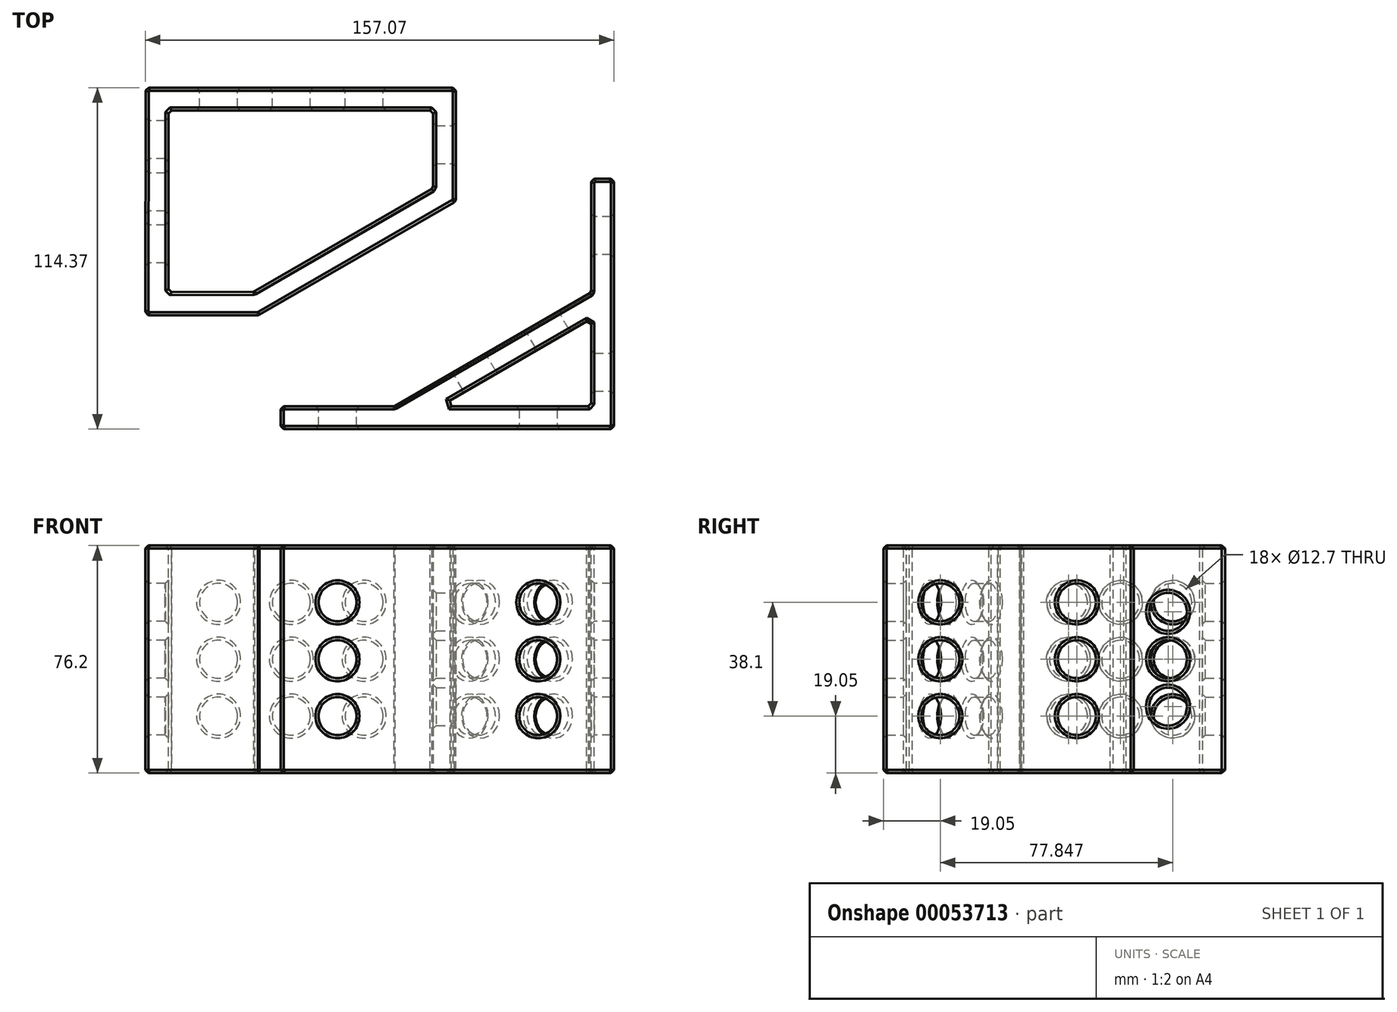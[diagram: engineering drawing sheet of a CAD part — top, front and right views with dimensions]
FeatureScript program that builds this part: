
annotation { "Feature Type Name" : "Feature", "Feature Type Description" : "" }
export const myFeature = defineFeature(function(context is Context, id is Id, definition is map)
    precondition{}
    {
        {
            var Q0;
            Q0=qCreatedBy(makeId("Top.planeOp"),FACE);
            var sketch = newSketch(context, id + "F0", { "sketchPlane" : qUnion([Q0])});
            skLineSegment(sketch, "E0", {"start": v(32.56, 38.1) * mm, "end": v(-33.43, 0) * mm});
            skLineSegment(sketch, "E1", {"start": v(-33.43, 0) * mm, "end": v(-71.53, 0) * mm});
            skLineSegment(sketch, "E2", {"start": v(-71.53, 0) * mm, "end": v(-71.53, -7.62) * mm});
            skLineSegment(sketch, "E3", {"start": v(-71.53, -7.62) * mm, "end": v(40.18, -7.62) * mm});
            skLineSegment(sketch, "E4", {"start": v(40.18, -7.62) * mm, "end": v(40.18, 76.2) * mm});
            skLineSegment(sketch, "E5", {"start": v(32.56, 38.1) * mm, "end": v(32.56, 76.2) * mm});
            skLineSegment(sketch, "E6", {"start": v(32.56, 76.2) * mm, "end": v(40.18, 76.2) * mm});
            skLineSegment(sketch, "E7", {"start": v(-3.8, 17.1) * mm, "end": v(0, 10.5) * mm, "construction": true});
            skLineSegment(sketch, "E8", {"start": v(-6.97, -7.62) * mm, "end": v(-6.97, 0) * mm, "construction": true});
            skLineSegment(sketch, "E9", {"start": v(40.18, 10.76) * mm, "end": v(32.56, 10.76) * mm, "construction": true});
            skLineSegment(sketch, "E10", {"start": v(32.56, 29.3) * mm, "end": v(-18.19, 0) * mm});
            skLineSegment(sketch, "E11", {"start": v(-18.19, 0) * mm, "end": v(32.56, 0) * mm});
            skLineSegment(sketch, "E12", {"start": v(32.56, 0) * mm, "end": v(32.56, 29.3) * mm});
            skSolve(sketch);
        }
        {
            var Q0;
            Q0=qCreatedBy(makeId("Top.planeOp"),FACE);
            var sketch = newSketch(context, id + "F1", { "sketchPlane" : qUnion([Q0])});
            skLineSegment(sketch, "E13", {"start": v(-12.8, 68.65) * mm, "end": v(-78.8, 30.55) * mm});
            skLineSegment(sketch, "E14", {"start": v(-78.8, 30.55) * mm, "end": v(-116.9, 30.55) * mm});
            skLineSegment(sketch, "E15", {"start": v(-12.8, 68.65) * mm, "end": v(-12.8, 106.75) * mm});
            skLineSegment(sketch, "E16", {"start": v(-12.8, 106.75) * mm, "end": v(-116.7, 106.75) * mm});
            skLineSegment(sketch, "E17", {"start": v(-116.7, 106.75) * mm, "end": v(-116.9, 30.55) * mm});
            skSolve(sketch);
        }
        {
            var Q0;
            Q0 = qSketchRegion(id + "F0", true);
            extrude(context, id + "F2", {"entities" : qUnion([Q0]), "depth" : 76.2 * mm});
        }
        {
            var Q0;
            Q0 = qSketchRegion(id + "F1", true);
            extrude(context, id + "F3", {"entities" : qUnion([Q0]), "depth" : 76.2 * mm});
        }
        {
            var Q0;
            Q0=makeQuery(id+"F3.opExtrude","CAP_FACE",FACE,{"disambiguationData":[OSD([sQuery(id+"F1.wireOp",EDGE,"E13"),sQuery(id+"F1.wireOp",EDGE,"E14"),sQuery(id+"F1.wireOp",EDGE,"E15"),sQuery(id+"F1.wireOp",EDGE,"E16"),sQuery(id+"F1.wireOp",EDGE,"E17")])],"isStart":false});
            var sketch = newSketch(context, id + "F4", { "sketchPlane" : qUnion([Q0])});
            skLineSegment(sketch, "E18", {"start": v(-64.75, 106.75) * mm, "end": v(-64.75, 99.13) * mm, "construction": true});
            skLineSegment(sketch, "E19", {"start": v(-116.78, 73.4) * mm, "end": v(-109.16, 73.37) * mm, "construction": true});
            skLineSegment(sketch, "E20", {"start": v(-97.84, 30.55) * mm, "end": v(-97.84, 38.17) * mm, "construction": true});
            skLineSegment(sketch, "E21", {"start": v(-12.8, 87.7) * mm, "end": v(-20.42, 87.7) * mm, "construction": true});
            skLineSegment(sketch, "E22", {"start": v(-45.8, 49.6) * mm, "end": v(-49.6, 56.2) * mm, "construction": true});
            skLineSegment(sketch, "E23", {"start": v(-64.75, 99.13) * mm, "end": v(-109.16, 99.13) * mm});
            skLineSegment(sketch, "E24", {"start": v(-109.16, 99.13) * mm, "end": v(-109.16, 38.17) * mm});
            skLineSegment(sketch, "E25", {"start": v(-64.75, 99.13) * mm, "end": v(-20.42, 99.13) * mm});
            skLineSegment(sketch, "E26", {"start": v(-20.42, 99.13) * mm, "end": v(-20.42, 73.05) * mm});
            skLineSegment(sketch, "E27", {"start": v(-20.42, 73.05) * mm, "end": v(-80.4, 38.42) * mm});
            skLineSegment(sketch, "E28", {"start": v(-109.16, 38.17) * mm, "end": v(-80.4, 38.42) * mm});
            skSolve(sketch);
        }
        {
            var Q0;
            Q0 = qSketchRegion(id + "F4", true);
            var Q1;
            Q1=makeQuery(id+"F3.opExtrude","CAP_FACE",FACE,{"disambiguationData":[OSD([sQuery(id+"F1.wireOp",EDGE,"E13"),sQuery(id+"F1.wireOp",EDGE,"E14"),sQuery(id+"F1.wireOp",EDGE,"E15"),sQuery(id+"F1.wireOp",EDGE,"E16"),sQuery(id+"F1.wireOp",EDGE,"E17")])],"isStart":true});
            extrude(context, id + "F5", {"entities" : qUnion([Q0]), "operationType" : NewBodyOperationType.REMOVE, "endBound" : BoundingType.UP_TO_SURFACE, "oppositeDirection" : true, "endBoundEntityFace" : qUnion([Q1]), "depth" : 25.4 * mm});
        }
        {
            var Q0;
            Q0=makeQuery(id+"F2.opExtrude","SWEPT_FACE",FACE,{"disambiguationData":[OSD([sQuery(id+"F0.wireOp",EDGE,"E0")])]});
            var sketch = newSketch(context, id + "F6", { "sketchPlane" : qUnion([Q0])});
            skLineSegment(sketch, "E29.bottom", {"start": v(28.95, 0) * mm, "end": v(-47.25, 0) * mm, "construction": true});
            skLineSegment(sketch, "E29.top", {"start": v(28.95, 76.2) * mm, "end": v(-47.25, 76.2) * mm, "construction": true});
            skLineSegment(sketch, "E29.left", {"start": v(28.95, 0) * mm, "end": v(28.95, 76.2) * mm, "construction": true});
            skLineSegment(sketch, "E29.right", {"start": v(-47.25, 0) * mm, "end": v(-47.25, 76.2) * mm, "construction": true});
            skLineSegment(sketch, "E30", {"start": v(-9.15, 0) * mm, "end": v(-9.15, 76.2) * mm, "construction": true});
            skLineSegment(sketch, "E31", {"start": v(28.95, 38.1) * mm, "end": v(-47.25, 38.1) * mm, "construction": true});
            skLineSegment(sketch, "E32", {"start": v(28.95, 38.1) * mm, "end": v(28.95, 0) * mm, "construction": true});
            skLineSegment(sketch, "E33", {"start": v(28.95, 19.05) * mm, "end": v(-47.25, 19.05) * mm, "construction": true});
            skLineSegment(sketch, "E34", {"start": v(28.95, 0) * mm, "end": v(-9.15, 0) * mm, "construction": true});
            skLineSegment(sketch, "E35", {"start": v(9.9, 0) * mm, "end": v(9.9, 76.2) * mm, "construction": true});
            skLineSegment(sketch, "E36", {"start": v(-9.15, 0) * mm, "end": v(-47.25, 0) * mm, "construction": true});
            skLineSegment(sketch, "E37", {"start": v(-28.2, 0) * mm, "end": v(-28.2, 76.2) * mm, "construction": true});
            skLineSegment(sketch, "E38", {"start": v(28.95, 38.1) * mm, "end": v(28.95, 76.2) * mm, "construction": true});
            skLineSegment(sketch, "E39", {"start": v(28.95, 57.15) * mm, "end": v(-47.25, 57.15) * mm, "construction": true});
            skCircle(sketch, "E40", {"center": v(-28.2, 57.15) * mm, "radius": 6.35 * mm});
            skCircle(sketch, "E41", {"center": v(-28.2, 38.1) * mm, "radius": 6.35 * mm});
            skCircle(sketch, "E42", {"center": v(-28.2, 19.05) * mm, "radius": 6.35 * mm});
            skLineSegment(sketch, "E43", {"start": v(0, 0) * mm, "end": v(0, 76.2) * mm, "construction": true});
            skCircle(sketch, "E44", {"center": v(0, 19.05) * mm, "radius": 6.35 * mm});
            skCircle(sketch, "E45", {"center": v(0, 38.1) * mm, "radius": 6.35 * mm});
            skCircle(sketch, "E46", {"center": v(0, 57.15) * mm, "radius": 6.35 * mm});
            skSolve(sketch);
        }
        {
            var Q0;
            Q0 = qSketchRegion(id + "F6", true);
            var Q1;
            Q1=makeQuery(id+"F2.opExtrude","SWEPT_FACE",FACE,{"disambiguationData":[OSD([sQuery(id+"F0.wireOp",EDGE,"E10")])]});
            extrude(context, id + "F7", {"entities" : qUnion([Q0]), "operationType" : NewBodyOperationType.REMOVE, "endBound" : BoundingType.UP_TO_SURFACE, "oppositeDirection" : true, "endBoundEntityFace" : qUnion([Q1]), "depth" : 25.4 * mm});
        }
        {
            var Q0;
            Q0=makeQuery(id+"F2.opExtrude","SWEPT_FACE",FACE,{"disambiguationData":[OSD([sQuery(id+"F0.wireOp",EDGE,"E1")])]});
            var sketch = newSketch(context, id + "F8", { "sketchPlane" : qUnion([Q0])});
            skLineSegment(sketch, "E47", {"start": v(71.53, 0) * mm, "end": v(52.48, 0) * mm, "construction": true});
            skLineSegment(sketch, "E48", {"start": v(52.48, 0) * mm, "end": v(33.43, 0) * mm, "construction": true});
            skLineSegment(sketch, "E49", {"start": v(33.43, 38.1) * mm, "end": v(33.43, 76.2) * mm, "construction": true});
            skLineSegment(sketch, "E50", {"start": v(33.43, 76.2) * mm, "end": v(52.48, 76.2) * mm, "construction": true});
            skLineSegment(sketch, "E51", {"start": v(52.48, 76.2) * mm, "end": v(71.53, 76.2) * mm, "construction": true});
            skLineSegment(sketch, "E52", {"start": v(71.53, 76.2) * mm, "end": v(71.53, 38.1) * mm, "construction": true});
            skLineSegment(sketch, "E53", {"start": v(71.53, 38.1) * mm, "end": v(71.53, 0) * mm, "construction": true});
            skLineSegment(sketch, "E54", {"start": v(52.48, 0) * mm, "end": v(52.48, 76.2) * mm, "construction": true});
            skLineSegment(sketch, "E55", {"start": v(71.53, 38.1) * mm, "end": v(33.43, 38.1) * mm, "construction": true});
            skLineSegment(sketch, "E56", {"start": v(33.43, 0) * mm, "end": v(33.43, 38.1) * mm, "construction": true});
            skLineSegment(sketch, "E57", {"start": v(33.43, 19.05) * mm, "end": v(71.53, 19.05) * mm, "construction": true});
            skLineSegment(sketch, "E58", {"start": v(71.53, 57.15) * mm, "end": v(33.43, 57.15) * mm, "construction": true});
            skCircle(sketch, "E59", {"center": v(52.48, 19.05) * mm, "radius": 6.35 * mm});
            skCircle(sketch, "E60", {"center": v(52.48, 38.1) * mm, "radius": 6.35 * mm});
            skCircle(sketch, "E61", {"center": v(52.48, 57.15) * mm, "radius": 6.35 * mm});
            skSolve(sketch);
        }
        {
            var Q0;
            Q0 = qSketchRegion(id + "F8", true);
            extrude(context, id + "F9", {"entities" : qUnion([Q0]), "operationType" : NewBodyOperationType.REMOVE, "oppositeDirection" : true, "depth" : 25.4 * mm});
        }
        {
            var Q0;
            Q0=makeQuery(id+"F2.opExtrude","SWEPT_FACE",FACE,{"disambiguationData":[OSD([sQuery(id+"F0.wireOp",EDGE,"E5")])]});
            var sketch = newSketch(context, id + "F10", { "sketchPlane" : qUnion([Q0])});
            skLineSegment(sketch, "E62", {"start": v(-38.1, 0) * mm, "end": v(-57.15, 0) * mm, "construction": true});
            skLineSegment(sketch, "E63", {"start": v(-57.15, 0) * mm, "end": v(-76.2, 0) * mm, "construction": true});
            skLineSegment(sketch, "E64", {"start": v(-76.2, 0) * mm, "end": v(-76.2, 38.1) * mm, "construction": true});
            skLineSegment(sketch, "E65", {"start": v(-76.2, 38.1) * mm, "end": v(-76.2, 76.2) * mm, "construction": true});
            skLineSegment(sketch, "E66", {"start": v(-76.2, 76.2) * mm, "end": v(-57.15, 76.2) * mm, "construction": true});
            skLineSegment(sketch, "E67", {"start": v(-57.15, 76.2) * mm, "end": v(-38.1, 76.2) * mm, "construction": true});
            skLineSegment(sketch, "E68", {"start": v(-38.1, 76.2) * mm, "end": v(-38.1, 38.1) * mm, "construction": true});
            skLineSegment(sketch, "E69", {"start": v(-38.1, 38.1) * mm, "end": v(-38.1, 0) * mm, "construction": true});
            skLineSegment(sketch, "E70", {"start": v(-57.15, 0) * mm, "end": v(-57.15, 76.2) * mm, "construction": true});
            skLineSegment(sketch, "E71", {"start": v(-38.1, 38.1) * mm, "end": v(-76.2, 38.1) * mm, "construction": true});
            skLineSegment(sketch, "E72", {"start": v(-76.2, 38.1) * mm, "end": v(-76.2, 0) * mm, "construction": true});
            skLineSegment(sketch, "E73", {"start": v(-76.2, 19.05) * mm, "end": v(-38.1, 19.05) * mm, "construction": true});
            skLineSegment(sketch, "E74", {"start": v(-38.1, 57.15) * mm, "end": v(-76.2, 57.15) * mm, "construction": true});
            skCircle(sketch, "E75", {"center": v(-57.15, 19.05) * mm, "radius": 6.35 * mm});
            skCircle(sketch, "E76", {"center": v(-57.15, 38.1) * mm, "radius": 6.35 * mm});
            skCircle(sketch, "E77", {"center": v(-57.15, 57.15) * mm, "radius": 6.35 * mm});
            skSolve(sketch);
        }
        {
            var Q0;
            Q0 = qSketchRegion(id + "F10", true);
            extrude(context, id + "F11", {"entities" : qUnion([Q0]), "operationType" : NewBodyOperationType.REMOVE, "oppositeDirection" : true, "depth" : 25.4 * mm});
        }
        {
            var Q0;
            Q0=makeQuery(id+"F2.opExtrude","SWEPT_FACE",FACE,{"disambiguationData":[OSD([sQuery(id+"F0.wireOp",EDGE,"E3")])]});
            var sketch = newSketch(context, id + "F12", { "sketchPlane" : qUnion([Q0])});
            skLineSegment(sketch, "E78", {"start": v(40.18, 76.2) * mm, "end": v(40.18, 38.1) * mm, "construction": true});
            skLineSegment(sketch, "E79", {"start": v(40.18, 38.1) * mm, "end": v(14.78, 38.1) * mm, "construction": true});
            skLineSegment(sketch, "E80", {"start": v(40.18, 0) * mm, "end": v(40.18, 38.1) * mm, "construction": true});
            skLineSegment(sketch, "E81", {"start": v(40.18, 19.05) * mm, "end": v(14.78, 19.05) * mm, "construction": true});
            skLineSegment(sketch, "E82", {"start": v(40.18, 38.1) * mm, "end": v(40.18, 57.15) * mm, "construction": true});
            skLineSegment(sketch, "E83", {"start": v(40.18, 57.15) * mm, "end": v(14.78, 57.15) * mm, "construction": true});
            skCircle(sketch, "E84", {"center": v(14.78, 19.05) * mm, "radius": 6.35 * mm});
            skCircle(sketch, "E85", {"center": v(14.78, 38.1) * mm, "radius": 6.35 * mm});
            skCircle(sketch, "E86", {"center": v(14.78, 57.15) * mm, "radius": 6.35 * mm});
            skSolve(sketch);
        }
        {
            var Q0;
            Q0 = qSketchRegion(id + "F12", true);
            var Q1;
            Q1=makeQuery(id+"F2.opExtrude","SWEPT_FACE",FACE,{"disambiguationData":[OSD([sQuery(id+"F0.wireOp",EDGE,"E11")])]});
            extrude(context, id + "F13", {"entities" : qUnion([Q0]), "operationType" : NewBodyOperationType.REMOVE, "endBound" : BoundingType.UP_TO_SURFACE, "oppositeDirection" : true, "endBoundEntityFace" : qUnion([Q1]), "depth" : 25.4 * mm});
        }
        {
            var Q0;
            Q0=makeQuery(id+"F2.opExtrude","SWEPT_FACE",FACE,{"disambiguationData":[OSD([sQuery(id+"F0.wireOp",EDGE,"E4")])]});
            var sketch = newSketch(context, id + "F14", { "sketchPlane" : qUnion([Q0])});
            skLineSegment(sketch, "E87", {"start": v(57.15, 57.15) * mm, "end": v(-7.62, 57.15) * mm, "construction": true});
            skLineSegment(sketch, "E88", {"start": v(57.15, 38.1) * mm, "end": v(-7.62, 38.1) * mm, "construction": true});
            skLineSegment(sketch, "E89", {"start": v(57.15, 19.05) * mm, "end": v(-7.62, 19.05) * mm, "construction": true});
            skLineSegment(sketch, "E90", {"start": v(-7.62, 76.2) * mm, "end": v(11.43, 76.2) * mm, "construction": true});
            skCircle(sketch, "E91", {"center": v(11.43, 57.15) * mm, "radius": 6.35 * mm});
            skPoint(sketch, "E91.centerSnap0", {"position": v(24.77, 57.15) * mm});
            skCircle(sketch, "E92", {"center": v(11.43, 38.1) * mm, "radius": 6.35 * mm});
            skCircle(sketch, "E93", {"center": v(11.43, 19.05) * mm, "radius": 6.35 * mm});
            skSolve(sketch);
        }
        {
            var Q0;
            Q0 = qSketchRegion(id + "F14", true);
            var Q1;
            Q1=makeQuery(id+"F2.opExtrude","SWEPT_FACE",FACE,{"disambiguationData":[OSD([sQuery(id+"F0.wireOp",EDGE,"E12")])]});
            extrude(context, id + "F15", {"entities" : qUnion([Q0]), "operationType" : NewBodyOperationType.REMOVE, "endBound" : BoundingType.UP_TO_SURFACE, "oppositeDirection" : true, "endBoundEntityFace" : qUnion([Q1]), "depth" : 25.4 * mm});
        }
        {
            var Q0;
            Q0=makeQuery(id+"F3.opExtrude","SWEPT_FACE",FACE,{"disambiguationData":[OSD([sQuery(id+"F1.wireOp",EDGE,"E15")])]});
            var sketch = newSketch(context, id + "F16", { "sketchPlane" : qUnion([Q0])});
            skLineSegment(sketch, "E94", {"start": v(106.75, 38.1) * mm, "end": v(68.65, 38.1) * mm, "construction": true});
            skLineSegment(sketch, "E95", {"start": v(106.75, 53.98) * mm, "end": v(68.65, 53.98) * mm, "construction": true});
            skLineSegment(sketch, "E96", {"start": v(68.65, 22.23) * mm, "end": v(106.75, 22.23) * mm, "construction": true});
            skCircle(sketch, "E97", {"center": v(87.7, 53.98) * mm, "radius": 6.35 * mm});
            skCircle(sketch, "E98", {"center": v(87.7, 38.1) * mm, "radius": 6.35 * mm});
            skCircle(sketch, "E99", {"center": v(87.7, 22.23) * mm, "radius": 6.35 * mm});
            skSolve(sketch);
        }
        {
            var Q0;
            Q0 = qSketchRegion(id + "F16", true);
            var Q1;
            Q1=makeQuery(id+"F5.boolean.opBoolean","COPY",FACE,{"derivedFrom":makeQuery(id+"F5.opExtrude","SWEPT_FACE",FACE,{"disambiguationData":[OSD([sQuery(id+"F4.wireOp",EDGE,"E26")])]})});
            extrude(context, id + "F17", {"entities" : qUnion([Q0]), "operationType" : NewBodyOperationType.REMOVE, "endBound" : BoundingType.UP_TO_SURFACE, "oppositeDirection" : true, "endBoundEntityFace" : qUnion([Q1]), "depth" : 25.4 * mm});
        }
        {
            var Q0;
            Q0=makeQuery(id+"F3.opExtrude","SWEPT_FACE",FACE,{"disambiguationData":[OSD([sQuery(id+"F1.wireOp",EDGE,"E16")])]});
            var sketch = newSketch(context, id + "F18", { "sketchPlane" : qUnion([Q0])});
            skLineSegment(sketch, "E100", {"start": v(116.7, 38.1) * mm, "end": v(116.7, 0) * mm, "construction": true});
            skLineSegment(sketch, "E101", {"start": v(92.3, 0) * mm, "end": v(92.3, 76.2) * mm, "construction": true});
            skLineSegment(sketch, "E102", {"start": v(43.54, 76.2) * mm, "end": v(43.54, 0) * mm, "construction": true});
            skLineSegment(sketch, "E103", {"start": v(64.75, 0) * mm, "end": v(64.75, 76.2) * mm, "construction": true});
            skLineSegment(sketch, "E104", {"start": v(116.7, 19.05) * mm, "end": v(19.15, 19.05) * mm, "construction": true});
            skLineSegment(sketch, "E105", {"start": v(116.7, 57.15) * mm, "end": v(19.15, 57.15) * mm, "construction": true});
            skLineSegment(sketch, "E106", {"start": v(116.7, 38.1) * mm, "end": v(19.15, 38.1) * mm, "construction": true});
            skCircle(sketch, "E107", {"center": v(92.3, 19.05) * mm, "radius": 6.35 * mm});
            skCircle(sketch, "E108", {"center": v(67.92, 19.05) * mm, "radius": 6.35 * mm});
            skCircle(sketch, "E109", {"center": v(43.54, 19.05) * mm, "radius": 6.35 * mm});
            skCircle(sketch, "E110", {"center": v(92.3, 38.1) * mm, "radius": 6.35 * mm});
            skCircle(sketch, "E111", {"center": v(67.92, 38.1) * mm, "radius": 6.35 * mm});
            skCircle(sketch, "E112", {"center": v(43.54, 38.1) * mm, "radius": 6.35 * mm});
            skCircle(sketch, "E113", {"center": v(92.3, 57.15) * mm, "radius": 6.35 * mm});
            skCircle(sketch, "E114", {"center": v(67.92, 57.15) * mm, "radius": 6.35 * mm});
            skCircle(sketch, "E115", {"center": v(43.54, 57.15) * mm, "radius": 6.35 * mm});
            skSolve(sketch);
        }
        {
            var Q0;
            Q0 = qSketchRegion(id + "F18", true);
            var Q1;
            Q1=makeQuery(id+"F5.boolean.opBoolean","COPY",FACE,{"derivedFrom":makeQuery(id+"F5.opExtrude","SWEPT_FACE",FACE,{"disambiguationData":[OSD([sQuery(id+"F4.wireOp",EDGE,"E23"),sQuery(id+"F4.wireOp",EDGE,"E25")])]})});
            extrude(context, id + "F19", {"entities" : qUnion([Q0]), "operationType" : NewBodyOperationType.REMOVE, "endBound" : BoundingType.UP_TO_SURFACE, "oppositeDirection" : true, "endBoundEntityFace" : qUnion([Q1]), "depth" : 25.4 * mm});
        }
        {
            var Q0;
            Q0=makeQuery(id+"F3.opExtrude","SWEPT_FACE",FACE,{"disambiguationData":[OSD([sQuery(id+"F1.wireOp",EDGE,"E17")])]});
            var sketch = newSketch(context, id + "F20", { "sketchPlane" : qUnion([Q0])});
            skCircle(sketch, "E116", {"center": v(-88.98, 19.05) * mm, "radius": 6.35 * mm});
            skCircle(sketch, "E117", {"center": v(-88.98, 38.1) * mm, "radius": 6.35 * mm});
            skCircle(sketch, "E118", {"center": v(-88.98, 57.15) * mm, "radius": 6.35 * mm});
            skCircle(sketch, "E119", {"center": v(-71.51, 19.05) * mm, "radius": 6.35 * mm});
            skCircle(sketch, "E120", {"center": v(-71.51, 38.1) * mm, "radius": 6.35 * mm});
            skCircle(sketch, "E121", {"center": v(-71.51, 57.15) * mm, "radius": 6.35 * mm});
            skCircle(sketch, "E122", {"center": v(-54.05, 19.05) * mm, "radius": 6.35 * mm});
            skCircle(sketch, "E123", {"center": v(-54.05, 38.1) * mm, "radius": 6.35 * mm});
            skCircle(sketch, "E124", {"center": v(-54.05, 57.15) * mm, "radius": 6.35 * mm});
            skSolve(sketch);
        }
        {
            var Q0;
            Q0 = qSketchRegion(id + "F20", true);
            var Q1;
            Q1=makeQuery(id+"F5.boolean.opBoolean","COPY",FACE,{"derivedFrom":makeQuery(id+"F5.opExtrude","SWEPT_FACE",FACE,{"disambiguationData":[OSD([sQuery(id+"F4.wireOp",EDGE,"E24")])]})});
            extrude(context, id + "F21", {"entities" : qUnion([Q0]), "operationType" : NewBodyOperationType.REMOVE, "endBound" : BoundingType.UP_TO_SURFACE, "oppositeDirection" : true, "endBoundEntityFace" : qUnion([Q1]), "depth" : 25.4 * mm});
        }
        {
            var Q0;
            Q0=makeQuery(id+"F17.boolean.opBoolean","COPY",FACE,{"derivedFrom":makeQuery(id+"F17.opExtrude","SWEPT_FACE",FACE,{"disambiguationData":[OSD([sQuery(id+"F16.wireOp",EDGE,"E99")])]})});
            var Q1;
            Q1=makeQuery(id+"F17.boolean.opBoolean","COPY",FACE,{"derivedFrom":makeQuery(id+"F17.opExtrude","SWEPT_FACE",FACE,{"disambiguationData":[OSD([sQuery(id+"F16.wireOp",EDGE,"E98")])]})});
            var Q2;
            Q2=makeQuery(id+"F17.boolean.opBoolean","COPY",FACE,{"derivedFrom":makeQuery(id+"F17.opExtrude","SWEPT_FACE",FACE,{"disambiguationData":[OSD([sQuery(id+"F16.wireOp",EDGE,"E97")])]})});
            chamfer(context, id + "F22", {"entities" : qUnion([Q0, Q1, Q2]), "width" : 1.02 * mm, "tangentPropagation" : true});
        }
        {
            var Q0;
            Q0=makeQuery(id+"F19.boolean.opBoolean","COPY",EDGE,{"derivedFrom":makeQuery(id+"F19.opExtrude","CAP_EDGE",EDGE,{"disambiguationData":[OSD([sQuery(id+"F18.wireOp",EDGE,"E115")])],"isStart":true})});
            var Q1;
            Q1=makeQuery(id+"F19.boolean.opBoolean","COPY",FACE,{"derivedFrom":makeQuery(id+"F19.opExtrude","SWEPT_FACE",FACE,{"disambiguationData":[OSD([sQuery(id+"F18.wireOp",EDGE,"E115")])]})});
            var Q2;
            Q2=makeQuery(id+"F19.boolean.opBoolean","COPY",FACE,{"derivedFrom":makeQuery(id+"F19.opExtrude","SWEPT_FACE",FACE,{"disambiguationData":[OSD([sQuery(id+"F18.wireOp",EDGE,"E114")])]})});
            var Q3;
            Q3=makeQuery(id+"F19.boolean.opBoolean","COPY",FACE,{"derivedFrom":makeQuery(id+"F19.opExtrude","SWEPT_FACE",FACE,{"disambiguationData":[OSD([sQuery(id+"F18.wireOp",EDGE,"E113")])]})});
            var Q4;
            Q4=makeQuery(id+"F19.boolean.opBoolean","COPY",FACE,{"derivedFrom":makeQuery(id+"F19.opExtrude","SWEPT_FACE",FACE,{"disambiguationData":[OSD([sQuery(id+"F18.wireOp",EDGE,"E110")])]})});
            var Q5;
            Q5=makeQuery(id+"F19.boolean.opBoolean","COPY",FACE,{"derivedFrom":makeQuery(id+"F19.opExtrude","SWEPT_FACE",FACE,{"disambiguationData":[OSD([sQuery(id+"F18.wireOp",EDGE,"E107")])]})});
            var Q6;
            Q6=makeQuery(id+"F19.boolean.opBoolean","COPY",FACE,{"derivedFrom":makeQuery(id+"F19.opExtrude","SWEPT_FACE",FACE,{"disambiguationData":[OSD([sQuery(id+"F18.wireOp",EDGE,"E111")])]})});
            var Q7;
            Q7=makeQuery(id+"F19.boolean.opBoolean","COPY",FACE,{"derivedFrom":makeQuery(id+"F19.opExtrude","SWEPT_FACE",FACE,{"disambiguationData":[OSD([sQuery(id+"F18.wireOp",EDGE,"E112")])]})});
            var Q8;
            Q8=makeQuery(id+"F19.boolean.opBoolean","COPY",FACE,{"derivedFrom":makeQuery(id+"F19.opExtrude","SWEPT_FACE",FACE,{"disambiguationData":[OSD([sQuery(id+"F18.wireOp",EDGE,"E109")])]})});
            var Q9;
            Q9=makeQuery(id+"F19.boolean.opBoolean","COPY",FACE,{"derivedFrom":makeQuery(id+"F19.opExtrude","SWEPT_FACE",FACE,{"disambiguationData":[OSD([sQuery(id+"F18.wireOp",EDGE,"E108")])]})});
            chamfer(context, id + "F23", {"entities" : qUnion([Q0, Q1, Q2, Q3, Q4, Q5, Q6, Q7, Q8, Q9]), "width" : 1.02 * mm, "tangentPropagation" : true});
        }
        {
            var Q0;
            Q0=makeQuery(id+"F21.boolean.opBoolean","COPY",FACE,{"derivedFrom":makeQuery(id+"F21.opExtrude","SWEPT_FACE",FACE,{"disambiguationData":[OSD([sQuery(id+"F20.wireOp",EDGE,"E122")])]})});
            var Q1;
            Q1=makeQuery(id+"F21.boolean.opBoolean","COPY",FACE,{"derivedFrom":makeQuery(id+"F21.opExtrude","SWEPT_FACE",FACE,{"disambiguationData":[OSD([sQuery(id+"F20.wireOp",EDGE,"E119")])]})});
            var Q2;
            Q2=makeQuery(id+"F21.boolean.opBoolean","COPY",FACE,{"derivedFrom":makeQuery(id+"F21.opExtrude","SWEPT_FACE",FACE,{"disambiguationData":[OSD([sQuery(id+"F20.wireOp",EDGE,"E116")])]})});
            var Q3;
            Q3=makeQuery(id+"F21.boolean.opBoolean","COPY",FACE,{"derivedFrom":makeQuery(id+"F21.opExtrude","SWEPT_FACE",FACE,{"disambiguationData":[OSD([sQuery(id+"F20.wireOp",EDGE,"E117")])]})});
            var Q4;
            Q4=makeQuery(id+"F21.boolean.opBoolean","COPY",FACE,{"derivedFrom":makeQuery(id+"F21.opExtrude","SWEPT_FACE",FACE,{"disambiguationData":[OSD([sQuery(id+"F20.wireOp",EDGE,"E120")])]})});
            var Q5;
            Q5=makeQuery(id+"F21.boolean.opBoolean","COPY",FACE,{"derivedFrom":makeQuery(id+"F21.opExtrude","SWEPT_FACE",FACE,{"disambiguationData":[OSD([sQuery(id+"F20.wireOp",EDGE,"E123")])]})});
            var Q6;
            Q6=makeQuery(id+"F21.boolean.opBoolean","COPY",FACE,{"derivedFrom":makeQuery(id+"F21.opExtrude","SWEPT_FACE",FACE,{"disambiguationData":[OSD([sQuery(id+"F20.wireOp",EDGE,"E124")])]})});
            var Q7;
            Q7=makeQuery(id+"F21.boolean.opBoolean","COPY",FACE,{"derivedFrom":makeQuery(id+"F21.opExtrude","SWEPT_FACE",FACE,{"disambiguationData":[OSD([sQuery(id+"F20.wireOp",EDGE,"E121")])]})});
            var Q8;
            Q8=makeQuery(id+"F21.boolean.opBoolean","COPY",FACE,{"derivedFrom":makeQuery(id+"F21.opExtrude","SWEPT_FACE",FACE,{"disambiguationData":[OSD([sQuery(id+"F20.wireOp",EDGE,"E118")])]})});
            chamfer(context, id + "F24", {"entities" : qUnion([Q0, Q1, Q2, Q3, Q4, Q5, Q6, Q7, Q8]), "width" : 1.02 * mm, "tangentPropagation" : true});
        }
        {
            var Q0;
            Q0=makeQuery(id+"F5.boolean.opBoolean","COPY",EDGE,{"derivedFrom":makeQuery(id+"F5.opExtrude","SWEPT_EDGE",EDGE,{"disambiguationData":[OSD([sQuery(id+"F4.wireOp",EDGE,"E24"),sQuery(id+"F4.wireOp",EDGE,"E28")])]})});
            var Q1;
            Q1=makeQuery(id+"F5.boolean.opBoolean","COPY",EDGE,{"derivedFrom":makeQuery(id+"F5.opExtrude","SWEPT_EDGE",EDGE,{"disambiguationData":[OSD([sQuery(id+"F4.wireOp",EDGE,"E27"),sQuery(id+"F4.wireOp",EDGE,"E28")])]})});
            var Q2;
            Q2=makeQuery(id+"F5.boolean.opBoolean","COPY",EDGE,{"derivedFrom":makeQuery(id+"F5.opExtrude","SWEPT_EDGE",EDGE,{"disambiguationData":[OSD([sQuery(id+"F4.wireOp",EDGE,"E26"),sQuery(id+"F4.wireOp",EDGE,"E27")])]})});
            var Q3;
            Q3=makeQuery(id+"F5.boolean.opBoolean","COPY",EDGE,{"derivedFrom":makeQuery(id+"F5.opExtrude","SWEPT_EDGE",EDGE,{"disambiguationData":[OSD([sQuery(id+"F4.wireOp",EDGE,"E25"),sQuery(id+"F4.wireOp",EDGE,"E26")])]})});
            var Q4;
            Q4=makeQuery(id+"F5.boolean.opBoolean","COPY",EDGE,{"derivedFrom":makeQuery(id+"F5.opExtrude","SWEPT_EDGE",EDGE,{"disambiguationData":[OSD([sQuery(id+"F4.wireOp",EDGE,"E23"),sQuery(id+"F4.wireOp",EDGE,"E24")])]})});
            chamfer(context, id + "F25", {"entities" : qUnion([Q0, Q1, Q2, Q3, Q4]), "width" : 1.02 * mm, "tangentPropagation" : true});
        }
        {
            var Q0;
            Q0=makeQuery(id+"F5.boolean.opBoolean","COPY",EDGE,{"derivedFrom":makeQuery(id+"F5.opExtrude","SWEPT_EDGE",EDGE,{"disambiguationData":[OSD([sQuery(id+"F4.wireOp",EDGE,"E25"),sQuery(id+"F4.wireOp",EDGE,"E26")])]})});
            var Q1;
            Q1=makeQuery(id+"F3.opExtrude","SWEPT_EDGE",EDGE,{"disambiguationData":[OSD([sQuery(id+"F1.wireOp",EDGE,"E14"),sQuery(id+"F1.wireOp",EDGE,"E17")])]});
            var Q2;
            Q2=makeQuery(id+"F3.opExtrude","SWEPT_EDGE",EDGE,{"disambiguationData":[OSD([sQuery(id+"F1.wireOp",EDGE,"E13"),sQuery(id+"F1.wireOp",EDGE,"E14")])]});
            var Q3;
            Q3=makeQuery(id+"F3.opExtrude","SWEPT_EDGE",EDGE,{"disambiguationData":[OSD([sQuery(id+"F1.wireOp",EDGE,"E13"),sQuery(id+"F1.wireOp",EDGE,"E15")])]});
            var Q4;
            Q4=makeQuery(id+"F5.boolean.opBoolean","COPY",EDGE,{"derivedFrom":makeQuery(id+"F5.opExtrude","SWEPT_EDGE",EDGE,{"disambiguationData":[OSD([sQuery(id+"F4.wireOp",EDGE,"E23"),sQuery(id+"F4.wireOp",EDGE,"E24")])]})});
            var Q5;
            Q5=makeQuery(id+"F3.opExtrude","SWEPT_EDGE",EDGE,{"disambiguationData":[OSD([sQuery(id+"F1.wireOp",EDGE,"E15"),sQuery(id+"F1.wireOp",EDGE,"E16")])]});
            var Q6;
            Q6=makeQuery(id+"F3.opExtrude","SWEPT_EDGE",EDGE,{"disambiguationData":[OSD([sQuery(id+"F1.wireOp",EDGE,"E16"),sQuery(id+"F1.wireOp",EDGE,"E17")])]});
            chamfer(context, id + "F26", {"entities" : qUnion([Q0, Q1, Q2, Q3, Q4, Q5, Q6]), "width" : 1.02 * mm, "tangentPropagation" : true});
        }
        {
            var Q0;
            Q0=makeQuery(id+"F3.opExtrude","CAP_FACE",FACE,{"disambiguationData":[OSD([sQuery(id+"F1.wireOp",EDGE,"E13"),sQuery(id+"F1.wireOp",EDGE,"E14"),sQuery(id+"F1.wireOp",EDGE,"E15"),sQuery(id+"F1.wireOp",EDGE,"E16"),sQuery(id+"F1.wireOp",EDGE,"E17")])],"isStart":false});
            var Q1;
            Q1=makeQuery(id+"F3.opExtrude","CAP_FACE",FACE,{"disambiguationData":[OSD([sQuery(id+"F1.wireOp",EDGE,"E13"),sQuery(id+"F1.wireOp",EDGE,"E14"),sQuery(id+"F1.wireOp",EDGE,"E15"),sQuery(id+"F1.wireOp",EDGE,"E16"),sQuery(id+"F1.wireOp",EDGE,"E17")])],"isStart":true});
            chamfer(context, id + "F27", {"entities" : qUnion([Q0, Q1]), "width" : 1.02 * mm, "tangentPropagation" : true});
        }
        {
            var Q0;
            Q0=makeQuery(id+"F9.boolean.opBoolean","COPY",FACE,{"derivedFrom":makeQuery(id+"F9.opExtrude","SWEPT_FACE",FACE,{"disambiguationData":[OSD([sQuery(id+"F8.wireOp",EDGE,"E59")])]})});
            var Q1;
            Q1=makeQuery(id+"F9.boolean.opBoolean","COPY",FACE,{"derivedFrom":makeQuery(id+"F9.opExtrude","SWEPT_FACE",FACE,{"disambiguationData":[OSD([sQuery(id+"F8.wireOp",EDGE,"E60")])]})});
            var Q2;
            Q2=makeQuery(id+"F9.boolean.opBoolean","COPY",FACE,{"derivedFrom":makeQuery(id+"F9.opExtrude","SWEPT_FACE",FACE,{"disambiguationData":[OSD([sQuery(id+"F8.wireOp",EDGE,"E61")])]})});
            chamfer(context, id + "F28", {"entities" : qUnion([Q0, Q1, Q2]), "width" : 1.02 * mm, "tangentPropagation" : true});
        }
        {
            var Q0;
            Q0=makeQuery(id+"F11.boolean.opBoolean","COPY",FACE,{"derivedFrom":makeQuery(id+"F11.opExtrude","SWEPT_FACE",FACE,{"disambiguationData":[OSD([sQuery(id+"F10.wireOp",EDGE,"E75")])]})});
            var Q1;
            Q1=makeQuery(id+"F11.boolean.opBoolean","COPY",FACE,{"derivedFrom":makeQuery(id+"F11.opExtrude","SWEPT_FACE",FACE,{"disambiguationData":[OSD([sQuery(id+"F10.wireOp",EDGE,"E76")])]})});
            var Q2;
            Q2=makeQuery(id+"F11.boolean.opBoolean","COPY",FACE,{"derivedFrom":makeQuery(id+"F11.opExtrude","SWEPT_FACE",FACE,{"disambiguationData":[OSD([sQuery(id+"F10.wireOp",EDGE,"E77")])]})});
            chamfer(context, id + "F29", {"entities" : qUnion([Q0, Q1, Q2]), "width" : 1.02 * mm, "tangentPropagation" : true});
        }
        {
            var Q0;
            Q0=makeQuery(id+"F15.boolean.opBoolean","COPY",FACE,{"derivedFrom":makeQuery(id+"F15.opExtrude","SWEPT_FACE",FACE,{"disambiguationData":[OSD([sQuery(id+"F14.wireOp",EDGE,"E91")])]})});
            var Q1;
            Q1=makeQuery(id+"F15.boolean.opBoolean","COPY",FACE,{"derivedFrom":makeQuery(id+"F15.opExtrude","SWEPT_FACE",FACE,{"disambiguationData":[OSD([sQuery(id+"F14.wireOp",EDGE,"E92")])]})});
            var Q2;
            Q2=makeQuery(id+"F15.boolean.opBoolean","COPY",FACE,{"derivedFrom":makeQuery(id+"F15.opExtrude","SWEPT_FACE",FACE,{"disambiguationData":[OSD([sQuery(id+"F14.wireOp",EDGE,"E93")])]})});
            chamfer(context, id + "F30", {"entities" : qUnion([Q0, Q1, Q2]), "width" : 1.02 * mm, "tangentPropagation" : true});
        }
        {
            var Q0;
            Q0=makeQuery(id+"F13.boolean.opBoolean","COPY",FACE,{"derivedFrom":makeQuery(id+"F13.opExtrude","SWEPT_FACE",FACE,{"disambiguationData":[OSD([sQuery(id+"F12.wireOp",EDGE,"E86")])]})});
            var Q1;
            Q1=makeQuery(id+"F13.boolean.opBoolean","COPY",FACE,{"derivedFrom":makeQuery(id+"F13.opExtrude","SWEPT_FACE",FACE,{"disambiguationData":[OSD([sQuery(id+"F12.wireOp",EDGE,"E85")])]})});
            var Q2;
            Q2=makeQuery(id+"F13.boolean.opBoolean","COPY",FACE,{"derivedFrom":makeQuery(id+"F13.opExtrude","SWEPT_FACE",FACE,{"disambiguationData":[OSD([sQuery(id+"F12.wireOp",EDGE,"E84")])]})});
            chamfer(context, id + "F31", {"entities" : qUnion([Q0, Q1, Q2]), "width" : 1.02 * mm, "tangentPropagation" : true});
        }
        {
            var Q0;
            Q0=makeQuery(id+"F7.boolean.opBoolean","COPY",FACE,{"derivedFrom":makeQuery(id+"F7.opExtrude","SWEPT_FACE",FACE,{"disambiguationData":[OSD([sQuery(id+"F6.wireOp",EDGE,"E42")])]})});
            var Q1;
            Q1=makeQuery(id+"F7.boolean.opBoolean","COPY",FACE,{"derivedFrom":makeQuery(id+"F7.opExtrude","SWEPT_FACE",FACE,{"disambiguationData":[OSD([sQuery(id+"F6.wireOp",EDGE,"E41")])]})});
            var Q2;
            Q2=makeQuery(id+"F7.boolean.opBoolean","COPY",FACE,{"derivedFrom":makeQuery(id+"F7.opExtrude","SWEPT_FACE",FACE,{"disambiguationData":[OSD([sQuery(id+"F6.wireOp",EDGE,"E40")])]})});
            var Q3;
            Q3=makeQuery(id+"F7.boolean.opBoolean","COPY",FACE,{"derivedFrom":makeQuery(id+"F7.opExtrude","SWEPT_FACE",FACE,{"disambiguationData":[OSD([sQuery(id+"F6.wireOp",EDGE,"E44")])]})});
            var Q4;
            Q4=makeQuery(id+"F7.boolean.opBoolean","COPY",FACE,{"derivedFrom":makeQuery(id+"F7.opExtrude","SWEPT_FACE",FACE,{"disambiguationData":[OSD([sQuery(id+"F6.wireOp",EDGE,"E45")])]})});
            var Q5;
            Q5=makeQuery(id+"F7.boolean.opBoolean","COPY",FACE,{"derivedFrom":makeQuery(id+"F7.opExtrude","SWEPT_FACE",FACE,{"disambiguationData":[OSD([sQuery(id+"F6.wireOp",EDGE,"E46")])]})});
            chamfer(context, id + "F32", {"entities" : qUnion([Q0, Q1, Q2, Q3, Q4, Q5]), "width" : 1.02 * mm, "tangentPropagation" : true});
        }
        {
            var Q0;
            Q0=makeQuery(id+"F2.opExtrude","SWEPT_EDGE",EDGE,{"disambiguationData":[OSD([sQuery(id+"F0.wireOp",EDGE,"E2"),sQuery(id+"F0.wireOp",EDGE,"E3")])]});
            var Q1;
            Q1=makeQuery(id+"F2.opExtrude","SWEPT_EDGE",EDGE,{"disambiguationData":[OSD([sQuery(id+"F0.wireOp",EDGE,"E1"),sQuery(id+"F0.wireOp",EDGE,"E2")])]});
            var Q2;
            Q2=makeQuery(id+"F2.opExtrude","SWEPT_EDGE",EDGE,{"disambiguationData":[OSD([sQuery(id+"F0.wireOp",EDGE,"E0"),sQuery(id+"F0.wireOp",EDGE,"E1")])]});
            var Q3;
            Q3=makeQuery(id+"F2.opExtrude","SWEPT_EDGE",EDGE,{"disambiguationData":[OSD([sQuery(id+"F0.wireOp",EDGE,"E0"),sQuery(id+"F0.wireOp",EDGE,"E5")])]});
            var Q4;
            Q4=makeQuery(id+"F2.opExtrude","SWEPT_EDGE",EDGE,{"disambiguationData":[OSD([sQuery(id+"F0.wireOp",EDGE,"E5"),sQuery(id+"F0.wireOp",EDGE,"E6")])]});
            var Q5;
            Q5=makeQuery(id+"F2.opExtrude","SWEPT_EDGE",EDGE,{"disambiguationData":[OSD([sQuery(id+"F0.wireOp",EDGE,"E4"),sQuery(id+"F0.wireOp",EDGE,"E6")])]});
            var Q6;
            Q6=makeQuery(id+"F2.opExtrude","SWEPT_EDGE",EDGE,{"disambiguationData":[OSD([sQuery(id+"F0.wireOp",EDGE,"E3"),sQuery(id+"F0.wireOp",EDGE,"E4")])]});
            chamfer(context, id + "F33", {"entities" : qUnion([Q0, Q1, Q2, Q3, Q4, Q5, Q6]), "width" : 1.02 * mm, "tangentPropagation" : true});
        }
        {
            var Q0;
            Q0=makeQuery(id+"F2.opExtrude","SWEPT_EDGE",EDGE,{"disambiguationData":[OSD([sQuery(id+"F0.wireOp",EDGE,"E11"),sQuery(id+"F0.wireOp",EDGE,"E12")])]});
            var Q1;
            Q1=makeQuery(id+"F2.opExtrude","SWEPT_EDGE",EDGE,{"disambiguationData":[OSD([sQuery(id+"F0.wireOp",EDGE,"E10"),sQuery(id+"F0.wireOp",EDGE,"E11")])]});
            chamfer(context, id + "F34", {"entities" : qUnion([Q0, Q1]), "width" : 1.02 * mm, "tangentPropagation" : true});
        }
        {
            var Q0;
            Q0=makeQuery(id+"F2.opExtrude","SWEPT_EDGE",EDGE,{"disambiguationData":[OSD([sQuery(id+"F0.wireOp",EDGE,"E10"),sQuery(id+"F0.wireOp",EDGE,"E12")])]});
            chamfer(context, id + "F35", {"entities" : qUnion([Q0]), "width" : 1.02 * mm, "tangentPropagation" : true});
        }
        {
            var Q0;
            Q0=makeQuery(id+"F2.opExtrude","CAP_FACE",FACE,{"disambiguationData":[OSD([sQuery(id+"F0.wireOp",EDGE,"E0"),sQuery(id+"F0.wireOp",EDGE,"E1"),sQuery(id+"F0.wireOp",EDGE,"E2"),sQuery(id+"F0.wireOp",EDGE,"E3"),sQuery(id+"F0.wireOp",EDGE,"E4"),sQuery(id+"F0.wireOp",EDGE,"E5"),sQuery(id+"F0.wireOp",EDGE,"E6"),sQuery(id+"F0.wireOp",EDGE,"E10"),sQuery(id+"F0.wireOp",EDGE,"E11"),sQuery(id+"F0.wireOp",EDGE,"E12")])],"isStart":true});
            var Q1;
            Q1=makeQuery(id+"F2.opExtrude","CAP_FACE",FACE,{"disambiguationData":[OSD([sQuery(id+"F0.wireOp",EDGE,"E0"),sQuery(id+"F0.wireOp",EDGE,"E1"),sQuery(id+"F0.wireOp",EDGE,"E2"),sQuery(id+"F0.wireOp",EDGE,"E3"),sQuery(id+"F0.wireOp",EDGE,"E4"),sQuery(id+"F0.wireOp",EDGE,"E5"),sQuery(id+"F0.wireOp",EDGE,"E6"),sQuery(id+"F0.wireOp",EDGE,"E10"),sQuery(id+"F0.wireOp",EDGE,"E11"),sQuery(id+"F0.wireOp",EDGE,"E12")])],"isStart":false});
            chamfer(context, id + "F36", {"entities" : qUnion([Q0, Q1]), "width" : 1.02 * mm, "tangentPropagation" : true});
        }
    });
